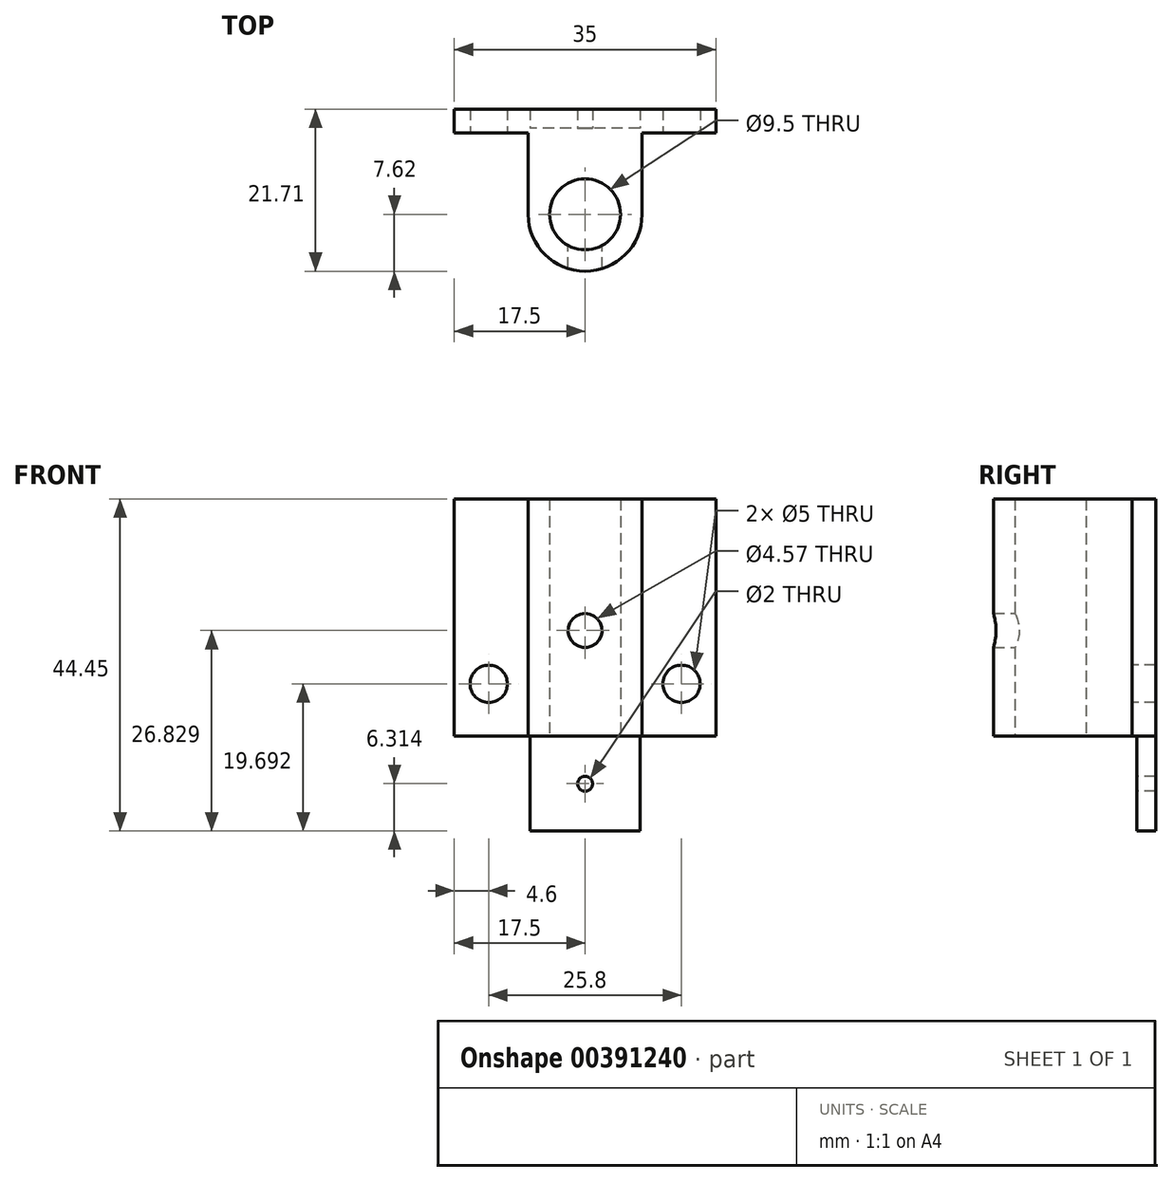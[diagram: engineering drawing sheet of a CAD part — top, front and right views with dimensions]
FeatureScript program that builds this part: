
annotation { "Feature Type Name" : "Feature", "Feature Type Description" : "" }
export const myFeature = defineFeature(function(context is Context, id is Id, definition is map)
    precondition{}
    {
        {
            var Q0;
            Q0=qCreatedBy(makeId("Top.planeOp"),FACE);
            var sketch = newSketch(context, id + "F0", { "sketchPlane" : qUnion([Q0])});
            skArc(sketch, "E0", {"start": v(-7.62, 0) * mm, "mid": v(0, -7.62) * mm, "end": v(7.62, 0) * mm});
            skLineSegment(sketch, "E1", {"start": v(-7.62, 0) * mm, "end": v(-7.62, 10.92) * mm});
            skLineSegment(sketch, "E2", {"start": v(7.62, 0) * mm, "end": v(7.62, 10.92) * mm});
            skPoint(sketch, "E3.startSnap0", {"position": v(-6.57, 10.92) * mm});
            skPoint(sketch, "E4.start.orphan", {"position": v(-5.53, 10.92) * mm});
            skLineSegment(sketch, "E5", {"start": v(-7.62, 10.92) * mm, "end": v(-17.5, 10.92) * mm});
            skLineSegment(sketch, "E6", {"start": v(-17.5, 10.92) * mm, "end": v(-17.5, 14.1) * mm});
            skLineSegment(sketch, "E7", {"start": v(-17.5, 14.1) * mm, "end": v(17.5, 14.1) * mm});
            skLineSegment(sketch, "E8", {"start": v(17.5, 14.1) * mm, "end": v(17.5, 10.92) * mm});
            skLineSegment(sketch, "E9", {"start": v(17.5, 10.92) * mm, "end": v(7.62, 10.92) * mm});
            skSolve(sketch);
        }
        {
            var Q0;
            Q0=makeQuery(id+"F0.imprint","IMPRINT",FACE,{"disambiguationData":[TD([[makeQuery(id+"F0.imprint","IMPRINT",EDGE,{"derivedFrom":sQuery(id+"F0.wireOp",EDGE,"aONOgf8h-lQvD-WjOp-fxbq-eSmup1vNnXjH")}),-1.0]])]});
            var Q1;
            Q1=makeQuery(id+"F0.imprint","IMPRINT",FACE,{"disambiguationData":[TD([[makeQuery(id+"F0.imprint","IMPRINT",EDGE,{"derivedFrom":sQuery(id+"F0.wireOp",EDGE,"aONOgf8h-lQvD-WjOp-fxbq-eSmup1vNnXjH")}),1.0]])]});
            var Q2;
            {var subQ1=sQuery(id+"F0.wireOp",EDGE,"E1");Q2=makeQuery(id+"F0.imprint","IMPRINT",FACE,{"disambiguationData":[TD([[makeQuery(id+"F0.imprint","IMPRINT",EDGE,{"derivedFrom":subQ1}),-1.0]])]});}
            extrude(context, id + "F1", {"entities" : qUnion([Q0, Q1, Q2]), "depth" : 31.75 * mm});
        }
        {
            var Q0;
            Q0=makeQuery(id+"F1.opExtrude","CAP_FACE",FACE,{"disambiguationData":[OSD([sQuery(id+"F0.wireOp",EDGE,"E0"),sQuery(id+"F0.wireOp",EDGE,"E1"),sQuery(id+"F0.wireOp",EDGE,"E2"),sQuery(id+"F0.wireOp",EDGE,"AFE0knfF-2ePD-CxW2-IbQb-XNOV47CSESSo"),sQuery(id+"F0.wireOp",EDGE,"E4"),sQuery(id+"F0.wireOp",EDGE,"E3"),sQuery(id+"F0.wireOp",EDGE,"AQ4WXuE7-N5so-tjZU-Vxsj-Ax7dbgLvQDCb"),sQuery(id+"F0.wireOp",EDGE,"xmKH7jiJ-YFLI-5Vtj-fnQD-N97nMyiYtLnw")])],"isStart":true});
            var sketch = newSketch(context, id + "F2", { "sketchPlane" : qUnion([Q0])});
            skCircle(sketch, "E10", {"center": v(0, 0) * mm, "radius": 4.75 * mm});
            skSolve(sketch);
        }
        {
            var Q0;
            Q0=makeQuery(id+"F2.imprint","IMPRINT",FACE,{"disambiguationData":[TD([[makeQuery(id+"F2.imprint","IMPRINT",EDGE,{"derivedFrom":sQuery(id+"F2.wireOp",EDGE,"E10")}),1.0]])]});
            extrude(context, id + "F3", {"entities" : qUnion([Q0]), "operationType" : NewBodyOperationType.REMOVE, "oppositeDirection" : true, "depth" : 38.1 * mm});
        }
        {
            var Q0;
            Q0=qCreatedBy(makeId("Front.planeOp"),FACE);
            var sketch = newSketch(context, id + "F4", { "sketchPlane" : qUnion([Q0])});
            skCircle(sketch, "E11", {"center": v(0, 14.13) * mm, "radius": 2.29 * mm});
            skSolve(sketch);
        }
        {
            var Q0;
            Q0=sQuery(id+"F4.wireOp",VERTEX,"E11.center");
            var Q1;
            Q1=makeQuery(id+"F1.opExtrude","SWEPT_BODY",BODY,{"disambiguationData":[OSD([sQuery(id+"F0.wireOp",EDGE,"E0"),sQuery(id+"F0.wireOp",EDGE,"E1"),sQuery(id+"F0.wireOp",EDGE,"E2"),sQuery(id+"F0.wireOp",EDGE,"AFE0knfF-2ePD-CxW2-IbQb-XNOV47CSESSo"),sQuery(id+"F0.wireOp",EDGE,"E4"),sQuery(id+"F0.wireOp",EDGE,"E3"),sQuery(id+"F0.wireOp",EDGE,"AQ4WXuE7-N5so-tjZU-Vxsj-Ax7dbgLvQDCb"),sQuery(id+"F0.wireOp",EDGE,"xmKH7jiJ-YFLI-5Vtj-fnQD-N97nMyiYtLnw")])]});
            hole(context, id + "F5", {"style" : HoleStyle.SIMPLE, "endStyle" : HoleEndStyle.THROUGH, "oppositeDirection" : true, "holeDiameter" : 4.57 * mm, "isTappedThrough" : true, "tappedDepth" : 12.7 * mm, "tapClearance" : 3, "locations" : qUnion([Q0]), "scope" : qUnion([Q1])});
        }
        {
            var Q0;
            Q0=makeQuery(id+"F1.opExtrude","CAP_FACE",FACE,{"disambiguationData":[OSD([sQuery(id+"F0.wireOp",EDGE,"E0"),sQuery(id+"F0.wireOp",EDGE,"E1"),sQuery(id+"F0.wireOp",EDGE,"E2"),sQuery(id+"F0.wireOp",EDGE,"E5"),sQuery(id+"F0.wireOp",EDGE,"E6"),sQuery(id+"F0.wireOp",EDGE,"E7"),sQuery(id+"F0.wireOp",EDGE,"E8"),sQuery(id+"F0.wireOp",EDGE,"E9")])],"isStart":true});
            var sketch = newSketch(context, id + "F6", { "sketchPlane" : qUnion([Q0])});
            skLineSegment(sketch, "E12.left", {"start": v(-7.34, -14.1) * mm, "end": v(-7.34, -11.55) * mm});
            skLineSegment(sketch, "E13", {"start": v(-7.34, -11.55) * mm, "end": v(0, -11.55) * mm});
            skLineSegment(sketch, "E14", {"start": v(-7.34, -14.1) * mm, "end": v(0, -14.1) * mm});
            skLineSegment(sketch, "E15", {"start": v(0, -11.55) * mm, "end": v(0, -14.1) * mm, "construction": true});
            skLineSegment(sketch, "E16.MirrorCS", {"start": v(7.34, -14.1) * mm, "end": v(7.34, -11.55) * mm});
            skLineSegment(sketch, "E17.MirrorCS", {"start": v(7.34, -11.55) * mm, "end": v(0, -11.55) * mm});
            skLineSegment(sketch, "E18.MirrorCS", {"start": v(7.34, -14.1) * mm, "end": v(0, -14.1) * mm});
            skSolve(sketch);
        }
        {
            var Q0;
            Q0=makeQuery(id+"F6.imprint","IMPRINT",FACE,{"disambiguationData":[TD([[makeQuery(id+"F6.imprint","IMPRINT",EDGE,{"derivedFrom":sQuery(id+"F6.wireOp",EDGE,"E12.left")}),-1.0]])]});
            extrude(context, id + "F7", {"entities" : qUnion([Q0]), "operationType" : NewBodyOperationType.ADD, "depth" : 12.7 * mm});
        }
        {
            var Q0;
            Q0=makeQuery(id+"F7.opExtrude","SWEPT_FACE",FACE,{"disambiguationData":[OSD([sQuery(id+"F6.wireOp",EDGE,"E13"),sQuery(id+"F6.wireOp",EDGE,"E17.MirrorCS")])]});
            var sketch = newSketch(context, id + "F8", { "sketchPlane" : qUnion([Q0])});
            skPoint(sketch, "E19", {"position": v(0, -6.39) * mm});
            skSolve(sketch);
        }
        {
            var Q0;
            Q0=sQuery(id+"F8.wireOp",VERTEX,"E19");
            var Q1;
            Q1=makeQuery(id+"F1.opExtrude","SWEPT_BODY",BODY,{"disambiguationData":[OSD([sQuery(id+"F0.wireOp",EDGE,"E0"),sQuery(id+"F0.wireOp",EDGE,"E1"),sQuery(id+"F0.wireOp",EDGE,"E2"),sQuery(id+"F0.wireOp",EDGE,"E5"),sQuery(id+"F0.wireOp",EDGE,"E6"),sQuery(id+"F0.wireOp",EDGE,"E7"),sQuery(id+"F0.wireOp",EDGE,"E8"),sQuery(id+"F0.wireOp",EDGE,"E9")])]});
            hole(context, id + "F9", {"style" : HoleStyle.SIMPLE, "endStyle" : HoleEndStyle.THROUGH, "holeDiameter" : 2 * mm, "isTappedThrough" : true, "tappedDepth" : 12 * mm, "tapClearance" : 3, "locations" : qUnion([Q0]), "scope" : qUnion([Q1])});
        }
        {
            var Q0;
            Q0=makeQuery(id+"F1.opExtrude","SWEPT_FACE",FACE,{"disambiguationData":[OSD([sQuery(id+"F0.wireOp",EDGE,"E5")])]});
            var sketch = newSketch(context, id + "F10", { "sketchPlane" : qUnion([Q0])});
            skPoint(sketch, "E20", {"position": v(-12.9, 7) * mm});
            skPoint(sketch, "E21", {"position": v(12.9, 7) * mm});
            skSolve(sketch);
        }
        {
            var Q0;
            Q0=sQuery(id+"F10.wireOp",VERTEX,"E20");
            var Q1;
            Q1=sQuery(id+"F10.wireOp",VERTEX,"E21");
            var Q2;
            Q2=makeQuery(id+"F1.opExtrude","SWEPT_BODY",BODY,{"disambiguationData":[OSD([sQuery(id+"F0.wireOp",EDGE,"E0"),sQuery(id+"F0.wireOp",EDGE,"E1"),sQuery(id+"F0.wireOp",EDGE,"E2"),sQuery(id+"F0.wireOp",EDGE,"E5"),sQuery(id+"F0.wireOp",EDGE,"E6"),sQuery(id+"F0.wireOp",EDGE,"E7"),sQuery(id+"F0.wireOp",EDGE,"E8"),sQuery(id+"F0.wireOp",EDGE,"E9")])]});
            hole(context, id + "F11", {"style" : HoleStyle.SIMPLE, "endStyle" : HoleEndStyle.THROUGH, "holeDiameter" : 5 * mm, "isTappedThrough" : true, "tappedDepth" : 12 * mm, "tapClearance" : 3, "locations" : qUnion([Q0, Q1]), "scope" : qUnion([Q2])});
        }
    });
